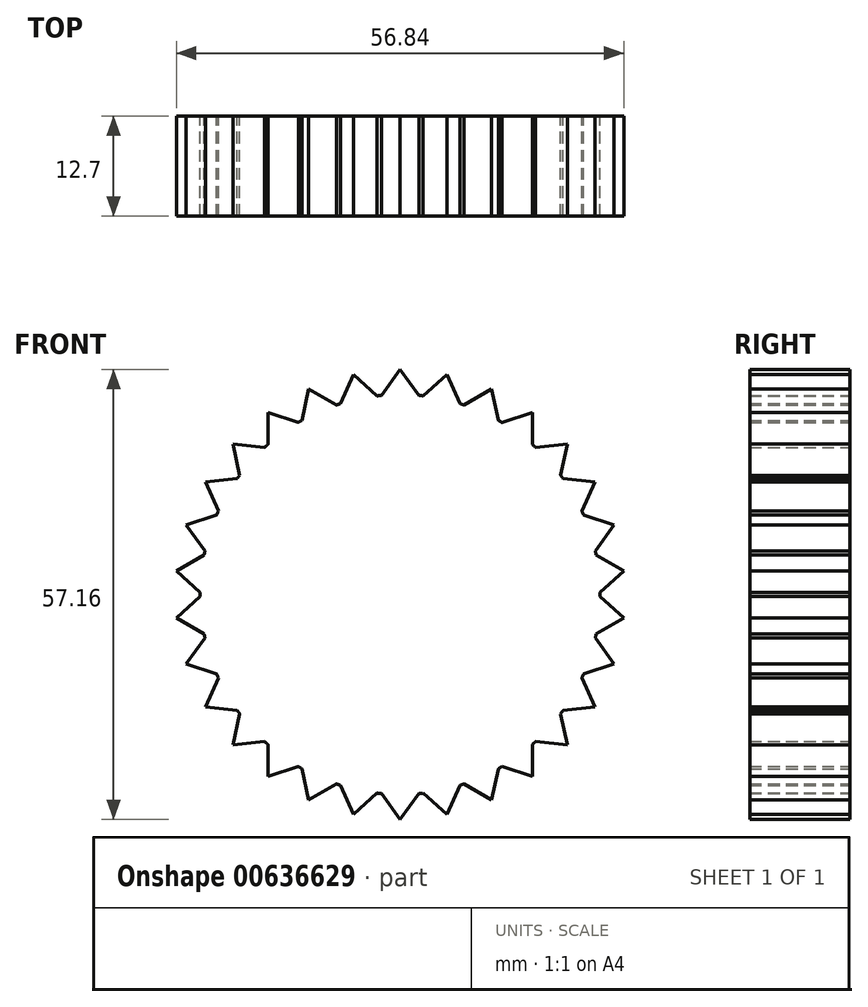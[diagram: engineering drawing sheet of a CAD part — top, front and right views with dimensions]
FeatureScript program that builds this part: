
annotation { "Feature Type Name" : "Feature", "Feature Type Description" : "" }
export const myFeature = defineFeature(function(context is Context, id is Id, definition is map)
    precondition{}
    {
        {
            var Q0;
            Q0=qCreatedBy(makeId("Front.planeOp"),FACE);
            var sketch = newSketch(context, id + "F0", { "sketchPlane" : qUnion([Q0])});
            skCircle(sketch, "E0", {"center": v(0, 0) * mm, "radius": 25.4 * mm});
            skLineSegment(sketch, "E1", {"start": v(0, 25.4) * mm, "end": v(0, 28.58) * mm});
            skLineSegment(sketch, "E2", {"start": v(0, 28.58) * mm, "end": v(-2.39, 25.29) * mm});
            skLineSegment(sketch, "E3.MirrorCS", {"start": v(0, 28.58) * mm, "end": v(2.39, 25.29) * mm});
            skLineSegment(sketch, "E4.1.0", {"start": v(-5.94, 27.95) * mm, "end": v(-7.6, 24.24) * mm});
            skLineSegment(sketch, "E4.1.1", {"start": v(-5.94, 27.95) * mm, "end": v(-2.92, 25.23) * mm});
            skLineSegment(sketch, "E4.2.0", {"start": v(-11.62, 26.1) * mm, "end": v(-12.46, 22.13) * mm});
            skLineSegment(sketch, "E4.2.1", {"start": v(-11.62, 26.1) * mm, "end": v(-8.1, 24.07) * mm});
            skLineSegment(sketch, "E4.3.0", {"start": v(-16.8, 23.12) * mm, "end": v(-16.8, 19.06) * mm});
            skLineSegment(sketch, "E4.3.1", {"start": v(-16.8, 23.12) * mm, "end": v(-12.93, 21.86) * mm});
            skLineSegment(sketch, "E4.4.0", {"start": v(-21.24, 19.12) * mm, "end": v(-20.39, 15.15) * mm});
            skLineSegment(sketch, "E4.4.1", {"start": v(-21.24, 19.12) * mm, "end": v(-17.2, 18.7) * mm});
            skLineSegment(sketch, "E4.5.0", {"start": v(-24.75, 14.29) * mm, "end": v(-23.1, 10.58) * mm});
            skLineSegment(sketch, "E4.5.1", {"start": v(-24.75, 14.29) * mm, "end": v(-20.7, 14.7) * mm});
            skLineSegment(sketch, "E4.6.0", {"start": v(-27.18, 8.83) * mm, "end": v(-24.79, 5.55) * mm});
            skLineSegment(sketch, "E4.6.1", {"start": v(-27.18, 8.83) * mm, "end": v(-23.31, 10.08) * mm});
            skLineSegment(sketch, "E4.7.0", {"start": v(-28.42, 2.99) * mm, "end": v(-25.4, 0.27) * mm});
            skLineSegment(sketch, "E4.7.1", {"start": v(-28.42, 2.99) * mm, "end": v(-24.9, 5.02) * mm});
            skLineSegment(sketch, "E4.8.0", {"start": v(-28.42, -2.99) * mm, "end": v(-24.9, -5.02) * mm});
            skLineSegment(sketch, "E4.8.1", {"start": v(-28.42, -2.99) * mm, "end": v(-25.4, -0.27) * mm});
            skLineSegment(sketch, "E4.9.0", {"start": v(-27.18, -8.83) * mm, "end": v(-23.31, -10.08) * mm});
            skLineSegment(sketch, "E4.9.1", {"start": v(-27.18, -8.83) * mm, "end": v(-24.79, -5.55) * mm});
            skLineSegment(sketch, "E4.10.0", {"start": v(-24.75, -14.29) * mm, "end": v(-20.7, -14.7) * mm});
            skLineSegment(sketch, "E4.10.1", {"start": v(-24.75, -14.29) * mm, "end": v(-23.1, -10.58) * mm});
            skLineSegment(sketch, "E4.11.0", {"start": v(-21.24, -19.12) * mm, "end": v(-17.2, -18.7) * mm});
            skLineSegment(sketch, "E4.11.1", {"start": v(-21.24, -19.12) * mm, "end": v(-20.39, -15.15) * mm});
            skLineSegment(sketch, "E4.12.0", {"start": v(-16.8, -23.12) * mm, "end": v(-12.93, -21.86) * mm});
            skLineSegment(sketch, "E4.12.1", {"start": v(-16.8, -23.12) * mm, "end": v(-16.8, -19.06) * mm});
            skLineSegment(sketch, "E4.13.0", {"start": v(-11.62, -26.1) * mm, "end": v(-8.1, -24.07) * mm});
            skLineSegment(sketch, "E4.13.1", {"start": v(-11.62, -26.1) * mm, "end": v(-12.46, -22.13) * mm});
            skLineSegment(sketch, "E4.14.0", {"start": v(-5.94, -27.95) * mm, "end": v(-2.92, -25.23) * mm});
            skLineSegment(sketch, "E4.14.1", {"start": v(-5.94, -27.95) * mm, "end": v(-7.6, -24.24) * mm});
            skLineSegment(sketch, "E4.15.0", {"start": v(0, -28.58) * mm, "end": v(2.39, -25.29) * mm});
            skLineSegment(sketch, "E4.15.1", {"start": v(0, -28.58) * mm, "end": v(-2.39, -25.29) * mm});
            skLineSegment(sketch, "E4.16.0", {"start": v(5.94, -27.95) * mm, "end": v(7.6, -24.24) * mm});
            skLineSegment(sketch, "E4.16.1", {"start": v(5.94, -27.95) * mm, "end": v(2.92, -25.23) * mm});
            skLineSegment(sketch, "E4.17.0", {"start": v(11.62, -26.1) * mm, "end": v(12.46, -22.13) * mm});
            skLineSegment(sketch, "E4.17.1", {"start": v(11.62, -26.1) * mm, "end": v(8.1, -24.07) * mm});
            skLineSegment(sketch, "E4.18.0", {"start": v(16.8, -23.12) * mm, "end": v(16.8, -19.06) * mm});
            skLineSegment(sketch, "E4.18.1", {"start": v(16.8, -23.12) * mm, "end": v(12.93, -21.86) * mm});
            skLineSegment(sketch, "E4.19.0", {"start": v(21.24, -19.12) * mm, "end": v(20.39, -15.15) * mm});
            skLineSegment(sketch, "E4.19.1", {"start": v(21.24, -19.12) * mm, "end": v(17.2, -18.7) * mm});
            skLineSegment(sketch, "E4.20.0", {"start": v(24.75, -14.29) * mm, "end": v(23.1, -10.58) * mm});
            skLineSegment(sketch, "E4.20.1", {"start": v(24.75, -14.29) * mm, "end": v(20.7, -14.7) * mm});
            skLineSegment(sketch, "E4.21.0", {"start": v(27.18, -8.83) * mm, "end": v(24.79, -5.55) * mm});
            skLineSegment(sketch, "E4.21.1", {"start": v(27.18, -8.83) * mm, "end": v(23.31, -10.08) * mm});
            skLineSegment(sketch, "E4.22.0", {"start": v(28.42, -2.99) * mm, "end": v(25.4, -0.27) * mm});
            skLineSegment(sketch, "E4.22.1", {"start": v(28.42, -2.99) * mm, "end": v(24.9, -5.02) * mm});
            skLineSegment(sketch, "E4.23.0", {"start": v(28.42, 2.99) * mm, "end": v(24.9, 5.02) * mm});
            skLineSegment(sketch, "E4.23.1", {"start": v(28.42, 2.99) * mm, "end": v(25.4, 0.27) * mm});
            skLineSegment(sketch, "E4.24.0", {"start": v(27.18, 8.83) * mm, "end": v(23.31, 10.08) * mm});
            skLineSegment(sketch, "E4.24.1", {"start": v(27.18, 8.83) * mm, "end": v(24.79, 5.55) * mm});
            skLineSegment(sketch, "E4.25.0", {"start": v(24.75, 14.29) * mm, "end": v(20.7, 14.7) * mm});
            skLineSegment(sketch, "E4.25.1", {"start": v(24.75, 14.29) * mm, "end": v(23.1, 10.58) * mm});
            skLineSegment(sketch, "E4.26.0", {"start": v(21.24, 19.12) * mm, "end": v(17.2, 18.7) * mm});
            skLineSegment(sketch, "E4.26.1", {"start": v(21.24, 19.12) * mm, "end": v(20.39, 15.15) * mm});
            skLineSegment(sketch, "E4.27.0", {"start": v(16.8, 23.12) * mm, "end": v(12.93, 21.86) * mm});
            skLineSegment(sketch, "E4.27.1", {"start": v(16.8, 23.12) * mm, "end": v(16.8, 19.06) * mm});
            skLineSegment(sketch, "E4.28.0", {"start": v(11.62, 26.1) * mm, "end": v(8.1, 24.07) * mm});
            skLineSegment(sketch, "E4.28.1", {"start": v(11.62, 26.1) * mm, "end": v(12.46, 22.13) * mm});
            skLineSegment(sketch, "E4.29.0", {"start": v(5.94, 27.95) * mm, "end": v(2.92, 25.23) * mm});
            skLineSegment(sketch, "E4.29.1", {"start": v(5.94, 27.95) * mm, "end": v(7.6, 24.24) * mm});
            skSolve(sketch);
        }
        {
            var Q0;
            Q0 = qSketchRegion(id + "F0", true);
            extrude(context, id + "F1", {"entities" : qUnion([Q0]), "depth" : 12.7 * mm, "offsetDistance" : 25.4 * mm});
        }
    });
